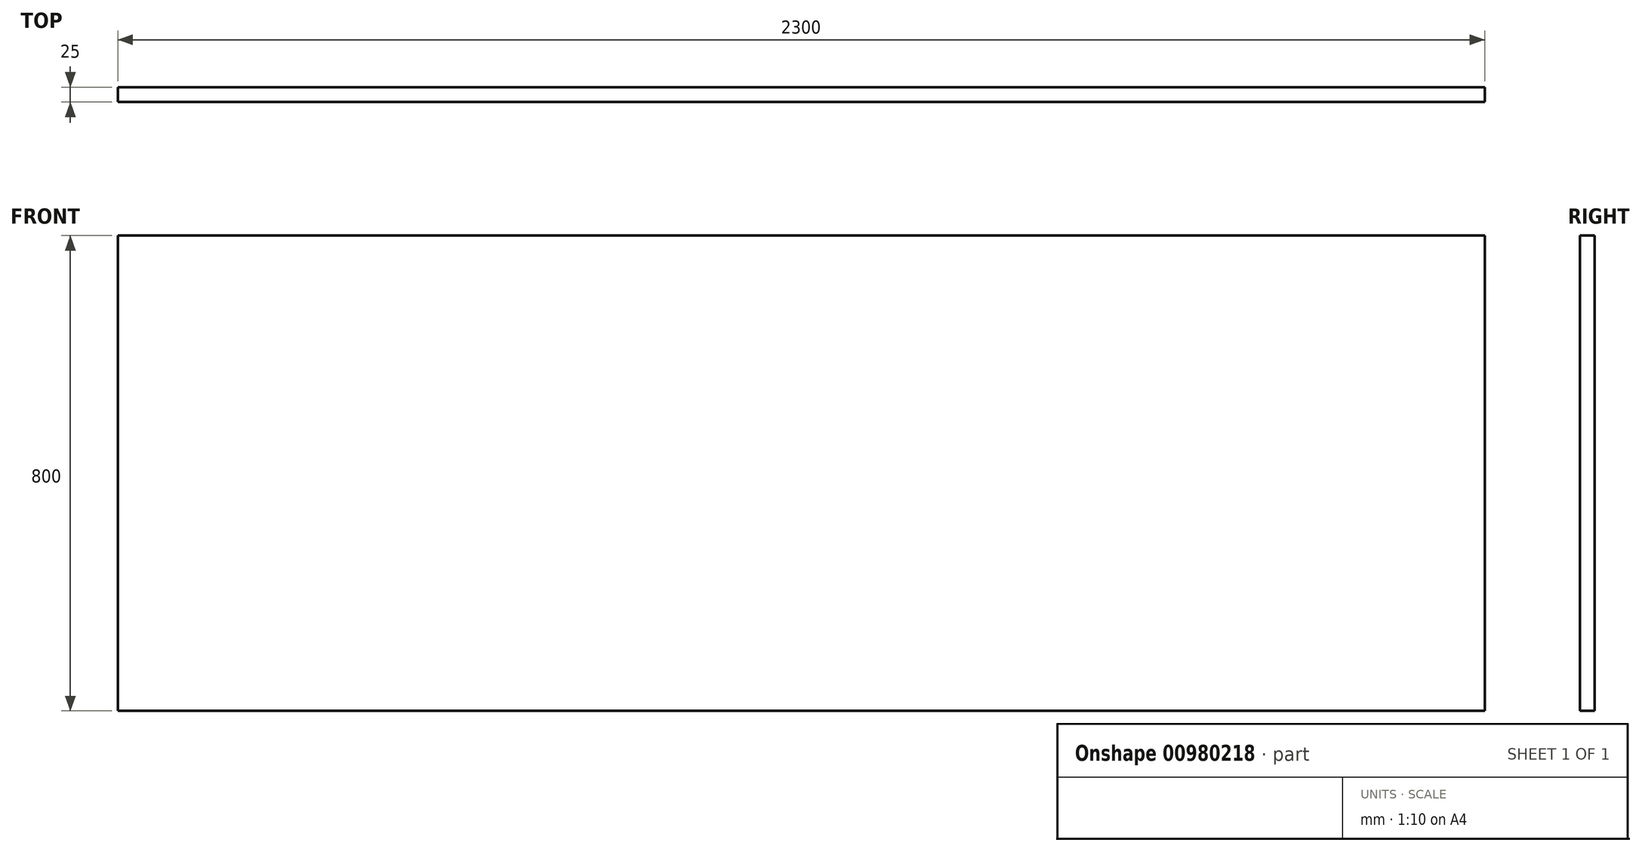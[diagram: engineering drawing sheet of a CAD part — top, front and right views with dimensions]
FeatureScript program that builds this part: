
annotation { "Feature Type Name" : "Feature", "Feature Type Description" : "" }
export const myFeature = defineFeature(function(context is Context, id is Id, definition is map)
    precondition{}
    {
        {
            var Q0;
            Q0=qCreatedBy(makeId("Front.planeOp"),FACE);
            var sketch = newSketch(context, id + "F0", { "sketchPlane" : qUnion([Q0])});
            skLineSegment(sketch, "E0.bottom", {"start": v(1150, 400) * mm, "end": v(-1150, 400) * mm});
            skLineSegment(sketch, "E0.top", {"start": v(1150, -400) * mm, "end": v(-1150, -400) * mm});
            skLineSegment(sketch, "E0.left", {"start": v(1150, 400) * mm, "end": v(1150, -400) * mm});
            skLineSegment(sketch, "E0.right", {"start": v(-1150, 400) * mm, "end": v(-1150, -400) * mm});
            skPoint(sketch, "E0.middle", {"position": v(0, 0) * mm});
            skSolve(sketch);
        }
        {
            var Q0;
            Q0=makeQuery(id+"F0.imprint","IMPRINT",FACE,{"disambiguationData":[TD([[makeQuery(id+"F0.imprint","IMPRINT",EDGE,{"derivedFrom":sQuery(id+"F0.wireOp",EDGE,"E0.bottom")}),1.0]])]});
            extrude(context, id + "F1", {"entities" : qUnion([Q0]), "depth" : 25 * mm, "offsetDistance" : 25 * mm});
        }
    });
